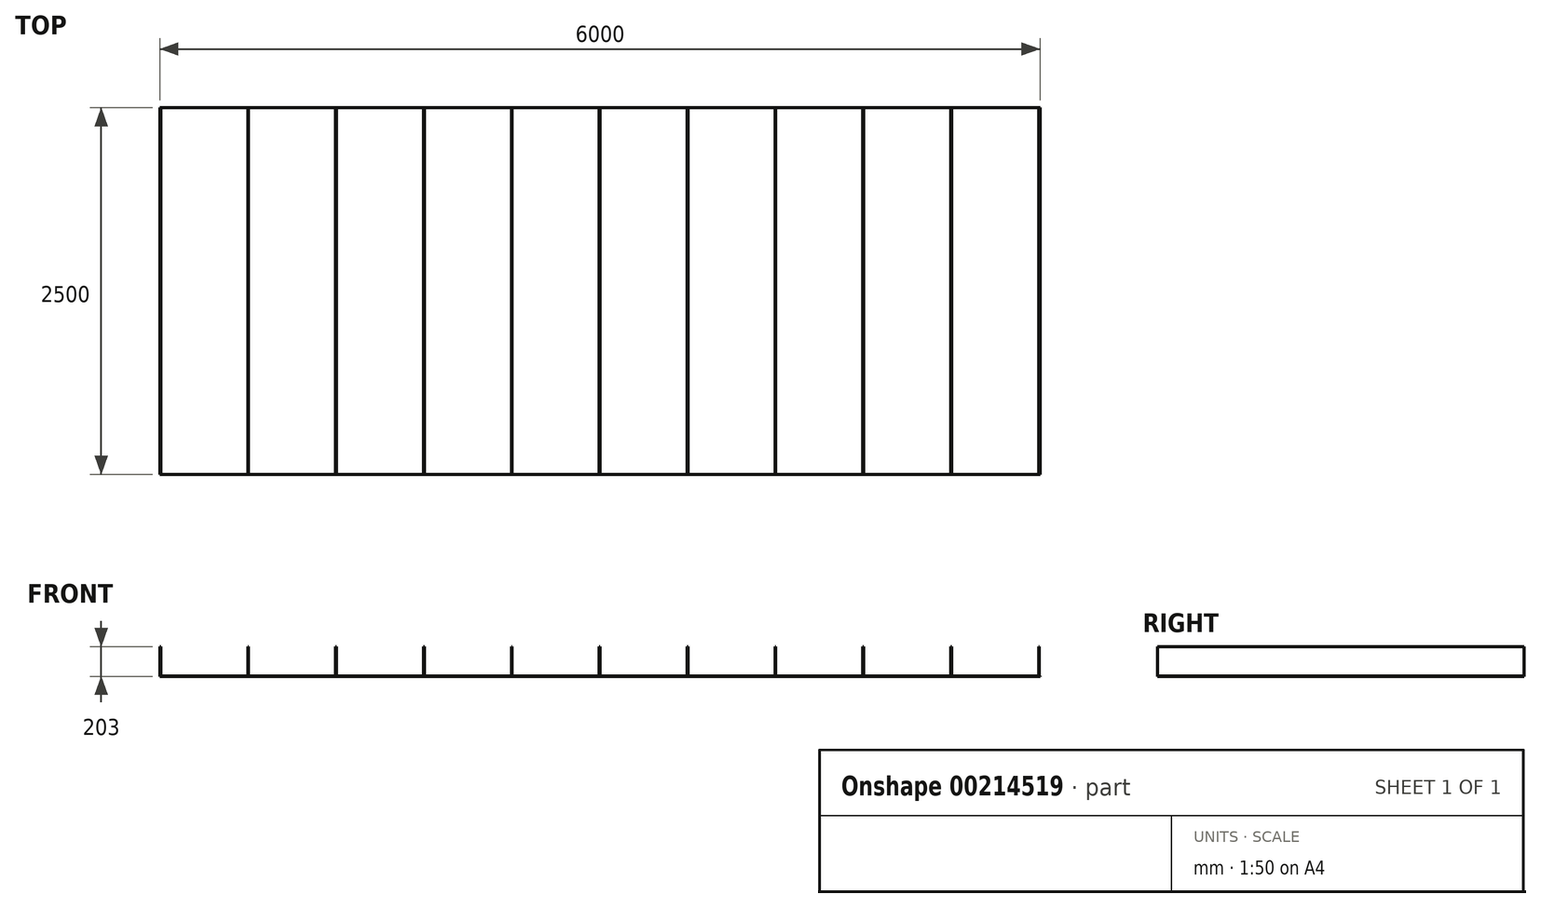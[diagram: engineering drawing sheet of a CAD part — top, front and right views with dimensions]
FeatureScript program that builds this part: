
annotation { "Feature Type Name" : "Feature", "Feature Type Description" : "" }
export const myFeature = defineFeature(function(context is Context, id is Id, definition is map)
    precondition{}
    {
        {
            var Q0;
            Q0=qCreatedBy(makeId("Front.planeOp"),FACE);
            var sketch = newSketch(context, id + "F0", { "sketchPlane" : qUnion([Q0])});
            skLineSegment(sketch, "E0.bottom", {"start": v(-3000, 11.21) * mm, "end": v(3000, 11.21) * mm});
            skLineSegment(sketch, "E0.top", {"start": v(-3000, 8.21) * mm, "end": v(3000, 8.21) * mm});
            skLineSegment(sketch, "E0.left", {"start": v(-3000, 11.21) * mm, "end": v(-3000, 8.21) * mm});
            skLineSegment(sketch, "E0.right", {"start": v(3000, 11.21) * mm, "end": v(3000, 8.21) * mm});
            skLineSegment(sketch, "E1.bottom", {"start": v(-3000, 11.21) * mm, "end": v(-2995, 11.21) * mm});
            skLineSegment(sketch, "E1.top", {"start": v(-3000, 211.21) * mm, "end": v(-2995, 211.21) * mm});
            skLineSegment(sketch, "E1.left", {"start": v(-3000, 11.21) * mm, "end": v(-3000, 211.21) * mm});
            skLineSegment(sketch, "E1.right", {"start": v(-2995, 11.21) * mm, "end": v(-2995, 211.21) * mm});
            skLineSegment(sketch, "E2.1.0.0", {"start": v(-2401, 211.21) * mm, "end": v(-2396, 211.21) * mm});
            skLineSegment(sketch, "E2.1.0.1", {"start": v(-2401, 11.21) * mm, "end": v(-2401, 211.21) * mm});
            skLineSegment(sketch, "E2.1.0.2", {"start": v(-2396, 11.21) * mm, "end": v(-2396, 211.21) * mm});
            skLineSegment(sketch, "E2.1.0.3", {"start": v(-2401, 8.21) * mm, "end": v(3599, 8.21) * mm});
            skLineSegment(sketch, "E2.2.0.0", {"start": v(-1802, 211.21) * mm, "end": v(-1797, 211.21) * mm});
            skLineSegment(sketch, "E2.2.0.1", {"start": v(-1802, 11.21) * mm, "end": v(-1802, 211.21) * mm});
            skLineSegment(sketch, "E2.2.0.2", {"start": v(-1797, 11.21) * mm, "end": v(-1797, 211.21) * mm});
            skLineSegment(sketch, "E2.2.0.3", {"start": v(-1802, 8.21) * mm, "end": v(4198, 8.21) * mm});
            skLineSegment(sketch, "E2.3.0.0", {"start": v(-1203, 211.21) * mm, "end": v(-1198, 211.21) * mm});
            skLineSegment(sketch, "E2.3.0.1", {"start": v(-1203, 11.21) * mm, "end": v(-1203, 211.21) * mm});
            skLineSegment(sketch, "E2.3.0.2", {"start": v(-1198, 11.21) * mm, "end": v(-1198, 211.21) * mm});
            skLineSegment(sketch, "E2.3.0.3", {"start": v(-1203, 8.21) * mm, "end": v(4797, 8.21) * mm});
            skLineSegment(sketch, "E2.4.0.0", {"start": v(-604, 211.21) * mm, "end": v(-599, 211.21) * mm});
            skLineSegment(sketch, "E2.4.0.1", {"start": v(-604, 11.21) * mm, "end": v(-604, 211.21) * mm});
            skLineSegment(sketch, "E2.4.0.2", {"start": v(-599, 11.21) * mm, "end": v(-599, 211.21) * mm});
            skLineSegment(sketch, "E2.4.0.3", {"start": v(-604, 8.21) * mm, "end": v(5396, 8.21) * mm});
            skLineSegment(sketch, "E2.5.0.0", {"start": v(-5, 211.21) * mm, "end": v(0, 211.21) * mm});
            skLineSegment(sketch, "E2.5.0.1", {"start": v(-5, 11.21) * mm, "end": v(-5, 211.21) * mm});
            skLineSegment(sketch, "E2.5.0.2", {"start": v(0, 11.21) * mm, "end": v(0, 211.21) * mm});
            skLineSegment(sketch, "E2.5.0.3", {"start": v(-5, 8.21) * mm, "end": v(5995, 8.21) * mm});
            skLineSegment(sketch, "E2.6.0.0", {"start": v(594, 211.21) * mm, "end": v(599, 211.21) * mm});
            skLineSegment(sketch, "E2.6.0.1", {"start": v(594, 11.21) * mm, "end": v(594, 211.21) * mm});
            skLineSegment(sketch, "E2.6.0.2", {"start": v(599, 11.21) * mm, "end": v(599, 211.21) * mm});
            skLineSegment(sketch, "E2.6.0.3", {"start": v(594, 8.21) * mm, "end": v(6594, 8.21) * mm});
            skLineSegment(sketch, "E2.7.0.0", {"start": v(1193, 211.21) * mm, "end": v(1198, 211.21) * mm});
            skLineSegment(sketch, "E2.7.0.1", {"start": v(1193, 11.21) * mm, "end": v(1193, 211.21) * mm});
            skLineSegment(sketch, "E2.7.0.2", {"start": v(1198, 11.21) * mm, "end": v(1198, 211.21) * mm});
            skLineSegment(sketch, "E2.7.0.3", {"start": v(1193, 8.21) * mm, "end": v(7193, 8.21) * mm});
            skLineSegment(sketch, "E2.8.0.0", {"start": v(1792, 211.21) * mm, "end": v(1797, 211.21) * mm});
            skLineSegment(sketch, "E2.8.0.1", {"start": v(1792, 11.21) * mm, "end": v(1792, 211.21) * mm});
            skLineSegment(sketch, "E2.8.0.2", {"start": v(1797, 11.21) * mm, "end": v(1797, 211.21) * mm});
            skLineSegment(sketch, "E2.8.0.3", {"start": v(1792, 8.21) * mm, "end": v(7792, 8.21) * mm});
            skLineSegment(sketch, "E2.9.0.0", {"start": v(2391, 211.21) * mm, "end": v(2396, 211.21) * mm});
            skLineSegment(sketch, "E2.9.0.1", {"start": v(2391, 11.21) * mm, "end": v(2391, 211.21) * mm});
            skLineSegment(sketch, "E2.9.0.2", {"start": v(2396, 11.21) * mm, "end": v(2396, 211.21) * mm});
            skLineSegment(sketch, "E2.9.0.3", {"start": v(2391, 8.21) * mm, "end": v(8391, 8.21) * mm});
            skLineSegment(sketch, "E2.direction1", {"start": v(-3000, 11.21) * mm, "end": v(-2401, 11.21) * mm, "construction": true});
            skLineSegment(sketch, "E3.0.10.0", {"start": v(2990, 211.21) * mm, "end": v(2995, 211.21) * mm});
            skLineSegment(sketch, "E3.3.10.0", {"start": v(2990, 11.21) * mm, "end": v(2990, 211.21) * mm});
            skLineSegment(sketch, "E3.6.10.0", {"start": v(2995, 11.21) * mm, "end": v(2995, 211.21) * mm});
            skSolve(sketch);
        }
        {
            var Q0;
            Q0 = qSketchRegion(id + "F0", true);
            extrude(context, id + "F1", {"entities" : qUnion([Q0]), "depth" : 2500 * mm});
        }
    });
